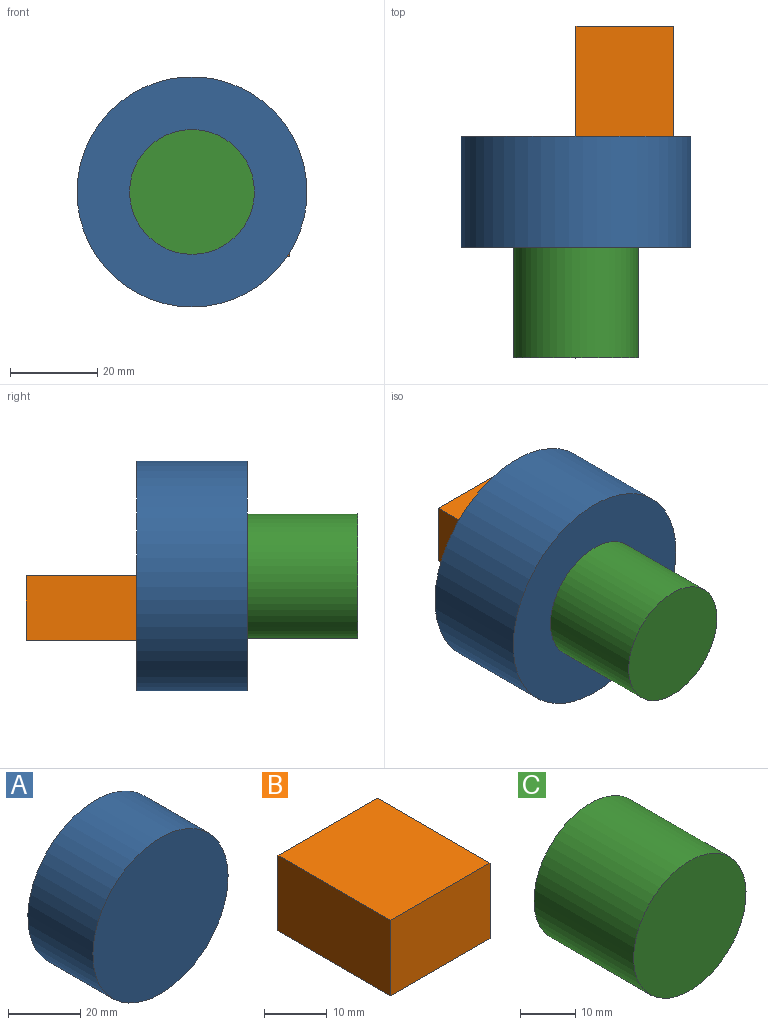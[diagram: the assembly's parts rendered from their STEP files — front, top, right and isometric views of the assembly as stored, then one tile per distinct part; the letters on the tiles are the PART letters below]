
ASSEMBLY  parts=3 mates=2
PART A: 3 faces, bbox 52.8x25.4x52.8 mm
  f0: cylinder r=26.41mm len=52.82mm, axis (0,1,0), area 4214.7mm2, adj f1,f2
  f1: plane 52.82x52.82mm, normal (0,-1,0), area 2191.1mm2, adj f0
  f2: plane 52.82x52.82mm, normal (0,1,0), area 2191.1mm2, adj f0
PART B: 6 faces, bbox 22.4x25.4x14.8 mm
  f0: plane 25.4x22.43mm, normal (0,0,1), area 569.8mm2, adj f1,f3,f4,f5
  f1: plane 25.4x14.76mm, normal (-1,0,0), area 374.9mm2, adj f0,f2,f4,f5
  f2: plane 25.4x22.43mm, normal (0,0,-1), area 569.8mm2, adj f1,f3,f4,f5
  f3: plane 25.4x14.76mm, normal (1,0,0), area 374.9mm2, adj f0,f2,f4,f5
  f4: plane 22.43x14.76mm, normal (0,-1,0), area 331.1mm2, adj f0,f1,f2,f3
  f5: plane 22.43x14.76mm, normal (0,1,0), area 331.1mm2, adj f0,f1,f2,f3
PART C: 3 faces, bbox 28.7x25.4x28.7 mm
  f0: cylinder r=14.33mm len=28.66mm, axis (0,1,0), area 2286.8mm2, adj f1,f2
  f1: plane 28.66x28.66mm, normal (0,-1,0), area 645mm2, adj f0
  f2: plane 28.66x28.66mm, normal (0,1,0), area 645mm2, adj f0
PLACE A rot(axis=(0,0,1),180deg) t=(58.02,0,91.83)mm
PLACE B t=(124.12,50.8,101.03)mm
PLACE C at identity
MATE revolute A.f0 <-> C.f0  axis (0,-1,0) through (132.64,0,122.93)mm
MATE fastened A.f0 <-> B.f4  axis (0,1,0) through (132.64,25.4,122.93)mm
